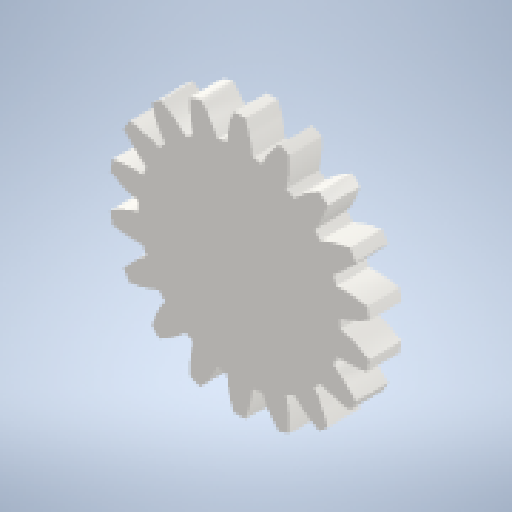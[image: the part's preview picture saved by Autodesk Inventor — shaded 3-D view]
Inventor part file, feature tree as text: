
AUTODESK INVENTOR PART (.ipt)
format: ipt  version: 2023 (Build 270158000, 158)  size: 287,232 bytes
history: native  units: mm (DEFAULTED — no unit token found)
features: extrude x4, sketch x3, plane x3, other x3, projected_geometry x1
ambient origin geometry x8: Origin, YZ Plane, XZ Plane, XY Plane, X Axis, Y Axis, Z Axis, Center Point
bodies: Solid1 (feature_tree)
feature tree (14):
  sketch  "Sketch1"  dims[d0=24.0mm d1=5.0mm d2=0.0mm]
  extrude  "Extrusion1"  Depth=5.0mm TaperAngle=0.0deg
  plane  "Work Plane2"
  plane  "Work Plane8"
  plane  "Work Plane9"
  other  "Spur Gear"
  extrude  "Extrusion2"  Depth=10.0mm TaperAngle=0.0deg
  sketch  "Sketch3"  dims[d16=40.0mm d17=0.0mm d34=3.141593mm d39=0.0mm d41=0.0mm d43=40.0mm d46=40.0mm d47=0.0mm d48=0.0mm d49=2.32mm d50=5.0mm d51=0.0mm d52=2.0mm d53=2.0mm d54=40.0mm d56=360.0deg d58=0.0mm d59=0.0mm d60=10.56mm d61=0.0mm]
  extrude  "Extrusion3"  Depth=10.56mm TaperAngle=0.0deg
  extrude  "Extrusion4"  TaperAngle=0.0deg  [1 undecoded]
  sketch  "Sketch2"  dims[d3=20.0mm d4=10.0mm d5=0.0mm]
  other  "Srf1"
  projected_geometry  "Projected Loop1"
  other  "Pitch Diameter"
note: 1 required parameter value undecoded (feature->parameter linkage not recoverable at this tier; creation-order binding heuristic only, values carry confidence <= 0.55)
